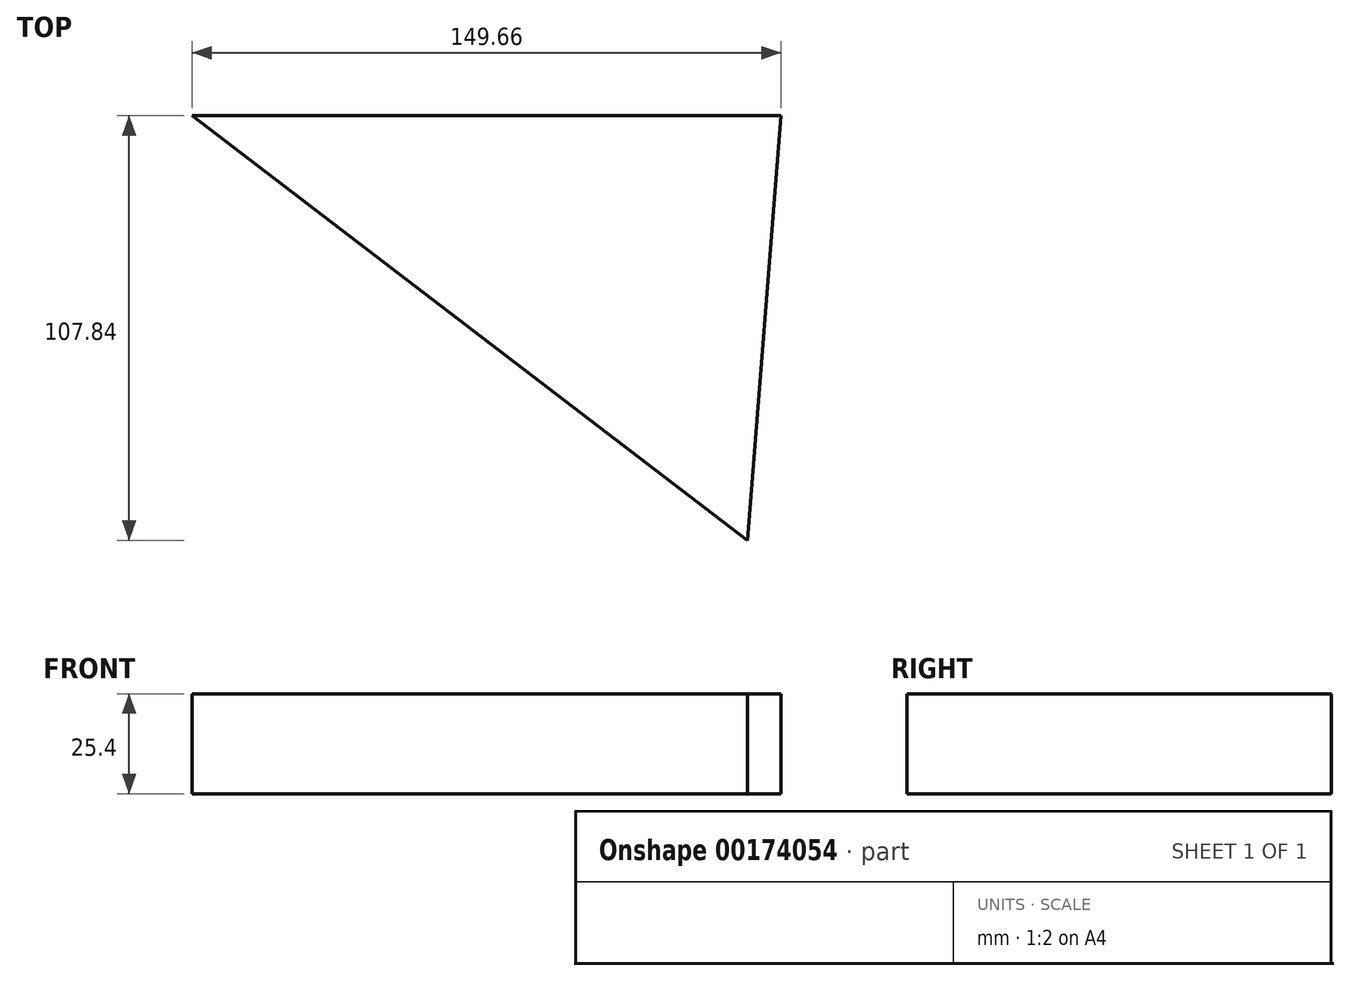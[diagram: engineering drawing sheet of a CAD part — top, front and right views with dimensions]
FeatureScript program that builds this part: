
annotation { "Feature Type Name" : "Feature", "Feature Type Description" : "" }
export const myFeature = defineFeature(function(context is Context, id is Id, definition is map)
    precondition{}
    {
        {
            var Q0;
            Q0=qCreatedBy(makeId("Top.planeOp"),FACE);
            var sketch = newSketch(context, id + "F0", { "sketchPlane" : qUnion([Q0])});
            skLineSegment(sketch, "E0", {"start": v(-141.07, 114.17) * mm, "end": v(8.6, 114.17) * mm});
            skLineSegment(sketch, "E1", {"start": v(8.6, 114.17) * mm, "end": v(0, 6.33) * mm});
            skLineSegment(sketch, "E2", {"start": v(0, 6.33) * mm, "end": v(-141.07, 114.17) * mm});
            skSolve(sketch);
        }
        {
            var Q0;
            Q0 = qSketchRegion(id + "F0", true);
            extrude(context, id + "F1", {"entities" : qUnion([Q0]), "depth" : 25.4 * mm});
        }
    });
